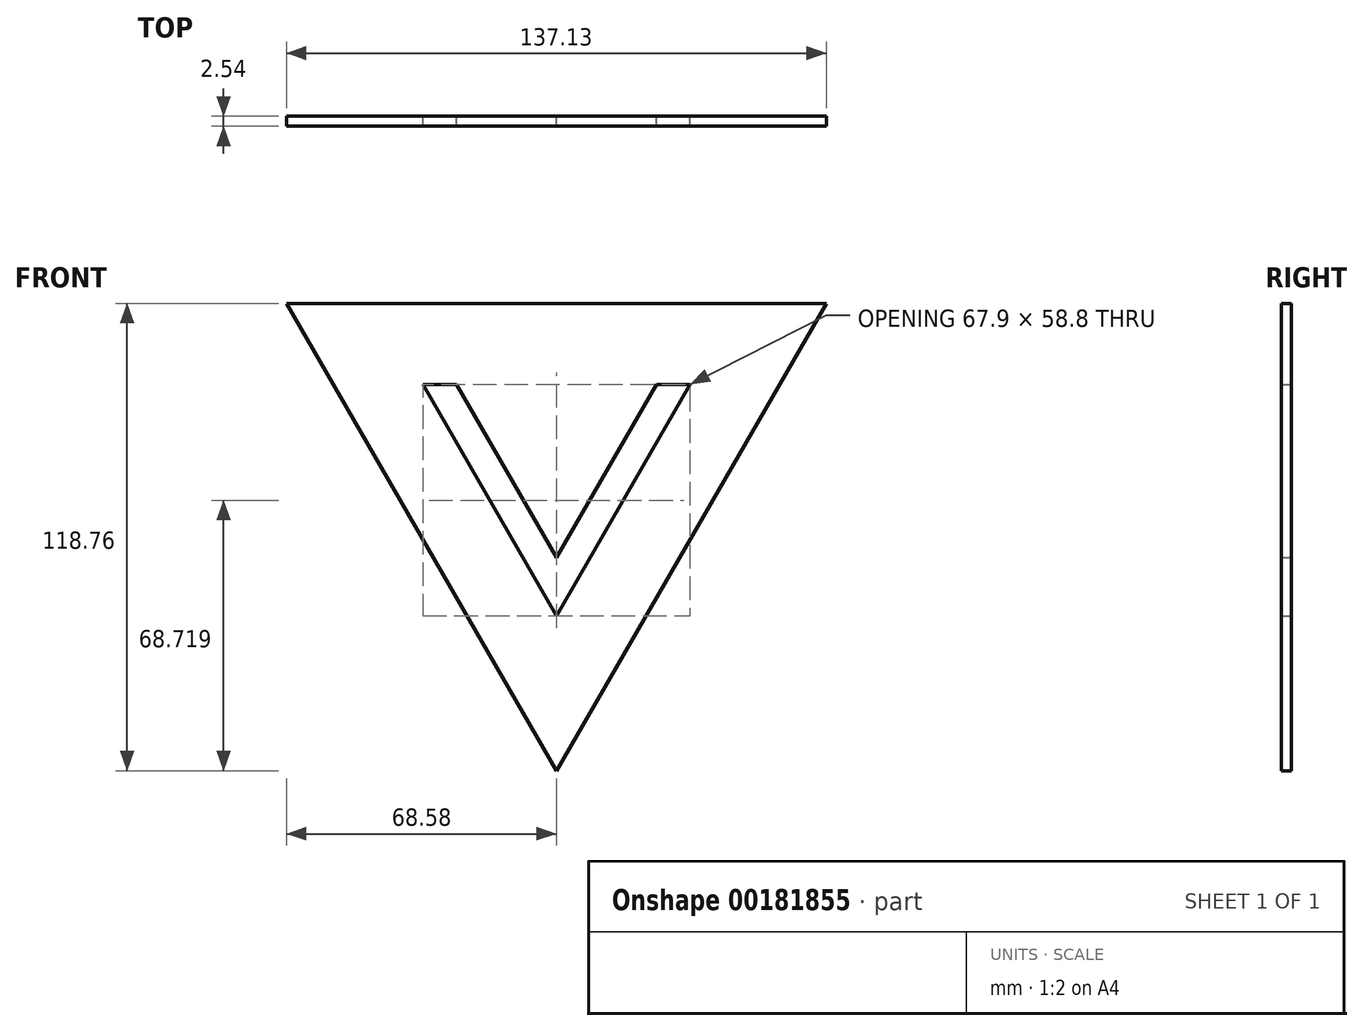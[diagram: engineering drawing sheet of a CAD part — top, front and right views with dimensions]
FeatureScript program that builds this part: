
annotation { "Feature Type Name" : "Feature", "Feature Type Description" : "" }
export const myFeature = defineFeature(function(context is Context, id is Id, definition is map)
    precondition{}
    {
        {
            var Q0;
            Q0=qCreatedBy(makeId("Front.planeOp"),FACE);
            var sketch = newSketch(context, id + "F0", { "sketchPlane" : qUnion([Q0])});
            skLineSegment(sketch, "E0", {"start": v(-33.95, 43.95) * mm, "end": v(33.95, 43.95) * mm});
            skLineSegment(sketch, "E1", {"start": v(33.95, 43.95) * mm, "end": v(0, -14.85) * mm});
            skLineSegment(sketch, "E2", {"start": v(0, -14.85) * mm, "end": v(-33.95, 43.95) * mm});
            skLineSegment(sketch, "E3", {"start": v(-68.58, 64.59) * mm, "end": v(68.55, 64.59) * mm});
            skLineSegment(sketch, "E4", {"start": v(68.55, 64.59) * mm, "end": v(-0.01, -54.17) * mm});
            skLineSegment(sketch, "E5", {"start": v(-68.58, 64.59) * mm, "end": v(-0.01, -54.17) * mm});
            skLineSegment(sketch, "E6", {"start": v(-25.38, 43.95) * mm, "end": v(0, 0) * mm});
            skLineSegment(sketch, "E7", {"start": v(0, 0) * mm, "end": v(25.38, 43.95) * mm});
            skSolve(sketch);
        }
        {
            var Q0;
            Q0 = qSketchRegion(id + "F0", true);
            extrude(context, id + "F1", {"entities" : qUnion([Q0]), "depth" : 2.54 * mm});
        }
        {
            var Q0;
            {var subQ0=sQuery(id+"F0.wireOp",EDGE,"E6");Q0=makeQuery(id+"F0.imprint","IMPRINT",FACE,{"disambiguationData":[TD([[makeQuery(id+"F0.imprint","IMPRINT",EDGE,{"derivedFrom":subQ0}),1.0]])]});}
            extrude(context, id + "F2", {"entities" : qUnion([Q0]), "operationType" : NewBodyOperationType.ADD, "depth" : 2.54 * mm});
        }
    });
